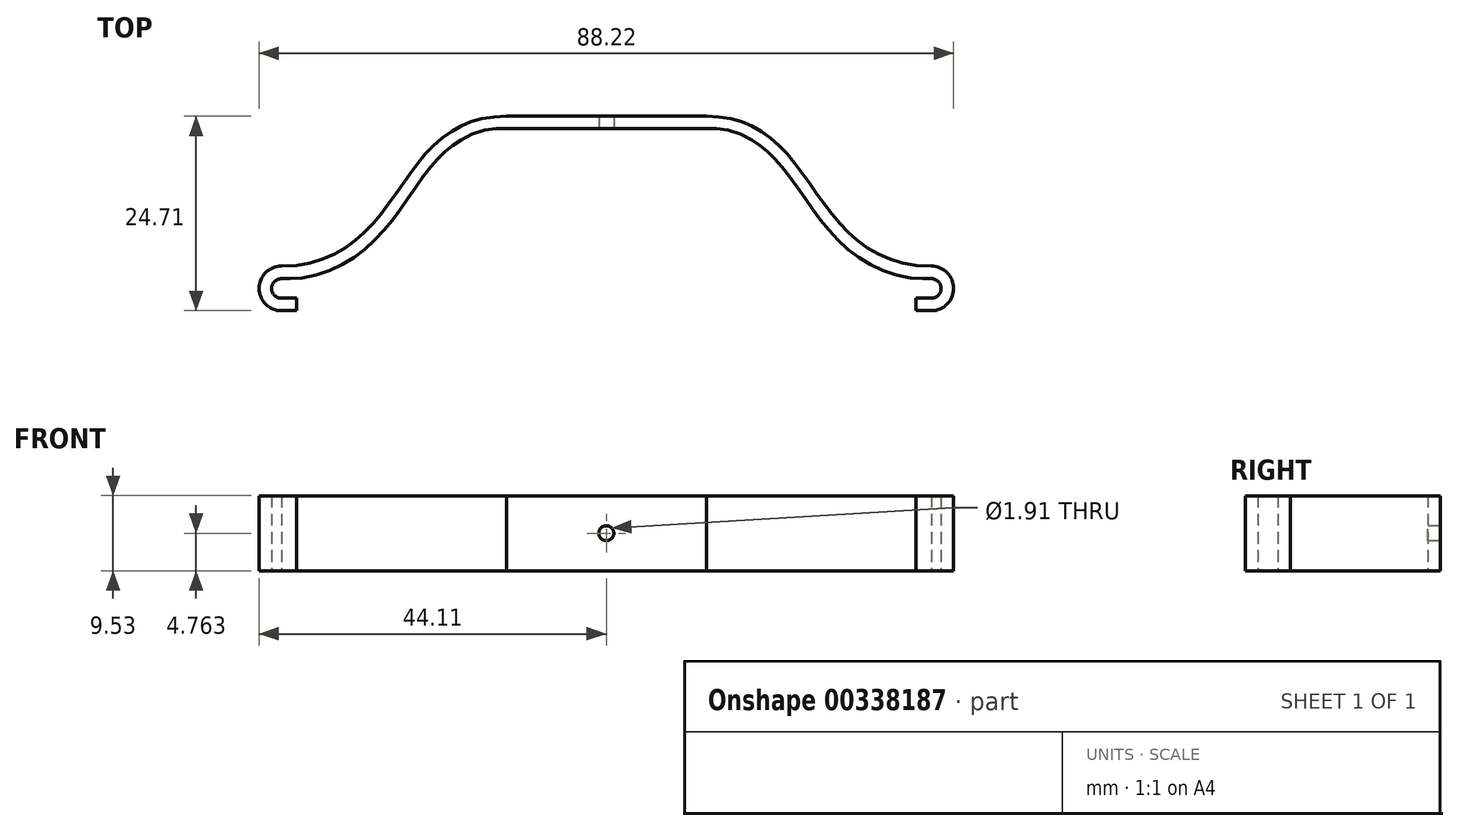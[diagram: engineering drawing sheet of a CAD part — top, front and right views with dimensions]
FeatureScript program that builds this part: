
annotation { "Feature Type Name" : "Feature", "Feature Type Description" : "" }
export const myFeature = defineFeature(function(context is Context, id is Id, definition is map)
    precondition{}
    {
        {
            var Q0;
            Q0=qCreatedBy(makeId("Top.planeOp"),FACE);
            var sketch = newSketch(context, id + "F0", { "sketchPlane" : qUnion([Q0])});
            skLineSegment(sketch, "E0", {"start": v(-12.7, 0) * mm, "end": v(12.7, 0) * mm});
            skLineSegment(sketch, "E1", {"start": v(0, 0) * mm, "end": v(0, -19.05) * mm, "construction": true});
            skLineSegment(sketch, "E2", {"start": v(-41.28, -19.05) * mm, "end": v(41.28, -19.05) * mm, "construction": true});
            skFitSpline(sketch, "E3", {"points": [v(-41.28, -19.05) * mm, v(-29.65, -13.6) * mm, v(-22.04, -3.8) * mm, v(-12.7, 0) * mm], "startDerivative": vector(45.55, 0) * mm, "endDerivative": vector(37.54, 0) * mm});
            skFitSpline(sketch, "E4.MirrorCS", {"points": [v(41.28, -19.05) * mm, v(29.65, -13.6) * mm, v(22.04, -3.8) * mm, v(12.7, 0) * mm], "startDerivative": vector(-45.55, 0) * mm, "endDerivative": vector(-37.54, 0) * mm});
            skFitSpline(sketch, "E5.0", {"points": [v(41.28, -20.64) * mm, v(40.24, -20.64) * mm, v(38.29, -20.48) * mm, v(35.64, -19.8) * mm, v(33.3, -18.73) * mm, v(31.22, -17.35) * mm, v(29.39, -15.71) * mm, v(27.76, -13.9) * mm, v(26.3, -11.98) * mm, v(24.95, -10.05) * mm, v(23.64, -8.18) * mm, v(22.34, -6.46) * mm, v(21.24, -5.22) * mm, v(20.32, -4.37) * mm, v(19.38, -3.6) * mm, v(18.14, -2.81) * mm, v(15.98, -1.89) * mm, v(14.11, -1.59) * mm, v(12.7, -1.59) * mm]});
            skLineSegment(sketch, "E5.1", {"start": v(-12.7, -1.59) * mm, "end": v(12.7, -1.59) * mm});
            skFitSpline(sketch, "E5.2", {"points": [v(-41.28, -20.64) * mm, v(-40.24, -20.64) * mm, v(-38.29, -20.48) * mm, v(-35.64, -19.8) * mm, v(-33.3, -18.73) * mm, v(-31.22, -17.35) * mm, v(-29.39, -15.71) * mm, v(-27.76, -13.9) * mm, v(-26.3, -11.98) * mm, v(-24.95, -10.05) * mm, v(-23.64, -8.18) * mm, v(-22.34, -6.46) * mm, v(-21.24, -5.22) * mm, v(-20.32, -4.37) * mm, v(-19.38, -3.6) * mm, v(-18.14, -2.81) * mm, v(-15.98, -1.89) * mm, v(-14.11, -1.59) * mm, v(-12.7, -1.59) * mm]});
            skLineSegment(sketch, "E6", {"start": v(-41.28, -23.13) * mm, "end": v(-39.32, -23.13) * mm});
            skArc(sketch, "E7", {"start": v(-41.28, -20.64) * mm, "mid": v(-42.52, -21.88) * mm, "end": v(-41.28, -23.13) * mm});
            skLineSegment(sketch, "E8.0", {"start": v(-41.28, -24.71) * mm, "end": v(-39.32, -24.71) * mm});
            skArc(sketch, "E8.1", {"start": v(-41.28, -19.05) * mm, "mid": v(-44.1, -21.88) * mm, "end": v(-41.28, -24.71) * mm});
            skLineSegment(sketch, "E9", {"start": v(-39.32, -24.71) * mm, "end": v(-39.32, -23.13) * mm});
            skArc(sketch, "E10.MirrorCS", {"start": v(41.28, -20.64) * mm, "mid": v(42.52, -21.88) * mm, "end": v(41.28, -23.13) * mm});
            skArc(sketch, "E11.MirrorCS", {"start": v(41.28, -19.05) * mm, "mid": v(44.1, -21.88) * mm, "end": v(41.28, -24.71) * mm});
            skLineSegment(sketch, "E12.MirrorCS", {"start": v(41.28, -24.71) * mm, "end": v(39.32, -24.71) * mm});
            skLineSegment(sketch, "E13.MirrorCS", {"start": v(39.32, -24.71) * mm, "end": v(39.32, -23.13) * mm});
            skLineSegment(sketch, "E14.MirrorCS", {"start": v(41.28, -23.13) * mm, "end": v(39.32, -23.13) * mm});
            skSolve(sketch);
        }
        {
            var Q0;
            Q0=makeQuery(id+"F0.imprint","IMPRINT",FACE,{"disambiguationData":[TD([[makeQuery(id+"F0.imprint","IMPRINT",EDGE,{"derivedFrom":sQuery(id+"F0.wireOp",EDGE,"E0")}),-1.0]])]});
            extrude(context, id + "F1", {"entities" : qUnion([Q0]), "depth" : 9.52 * mm});
        }
        {
            var Q0;
            Q0=makeQuery(id+"F1.opExtrude","SWEPT_FACE",FACE,{"disambiguationData":[OSD([sQuery(id+"F0.wireOp",EDGE,"E5.1")])]});
            var sketch = newSketch(context, id + "F2", { "sketchPlane" : qUnion([Q0])});
            skCircle(sketch, "E15", {"center": v(0, 4.76) * mm, "radius": 0.95 * mm});
            skPoint(sketch, "E15.centerSnap0", {"position": v(-12.7, 4.76) * mm});
            skSolve(sketch);
        }
        {
            var Q0;
            Q0 = qSketchRegion(id + "F2", true);
            extrude(context, id + "F3", {"entities" : qUnion([Q0]), "operationType" : NewBodyOperationType.REMOVE, "endBound" : BoundingType.THROUGH_ALL, "oppositeDirection" : true, "depth" : 25.4 * mm});
        }
    });
